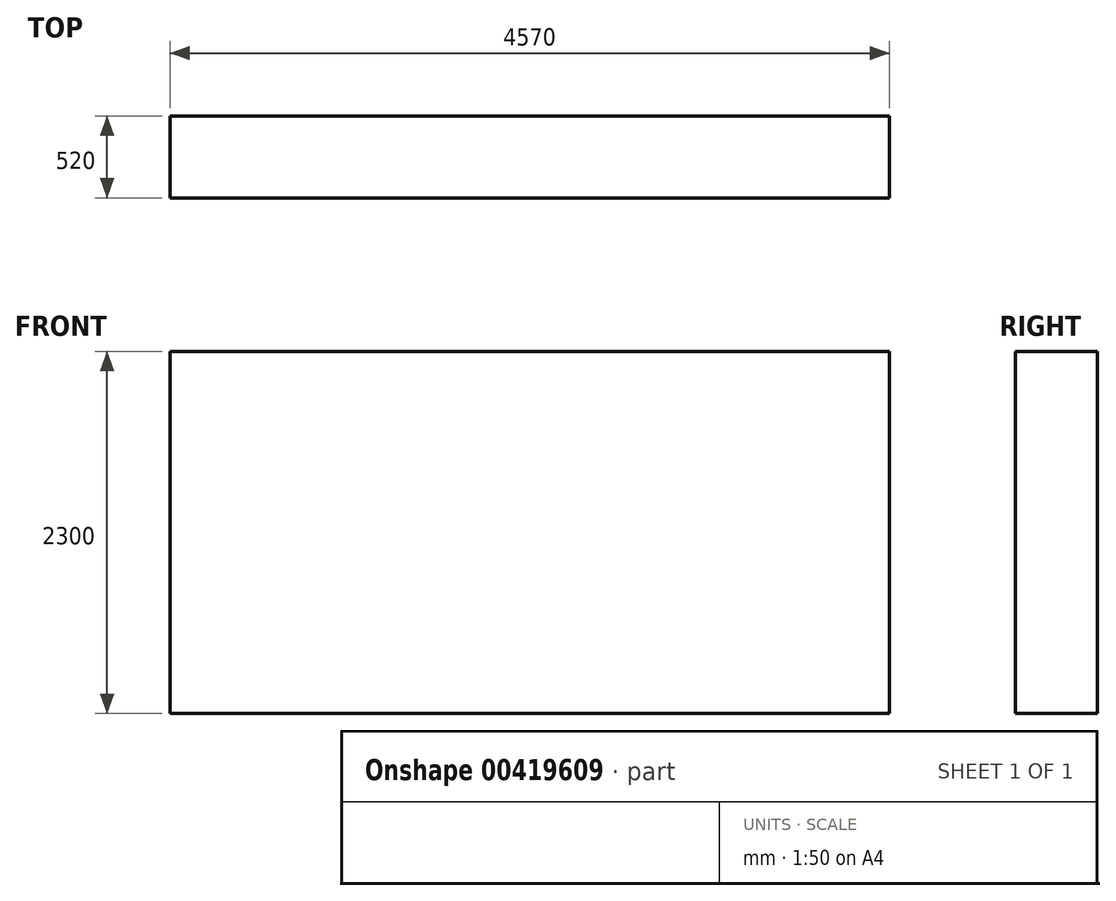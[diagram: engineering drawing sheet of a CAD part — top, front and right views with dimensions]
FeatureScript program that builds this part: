
annotation { "Feature Type Name" : "Feature", "Feature Type Description" : "" }
export const myFeature = defineFeature(function(context is Context, id is Id, definition is map)
    precondition{}
    {
        {
            var Q0;
            Q0=qCreatedBy(makeId("Top.planeOp"),FACE);
            var sketch = newSketch(context, id + "F0", { "sketchPlane" : qUnion([Q0])});
            skLineSegment(sketch, "E0.bottom", {"start": v(-4448.4, 487.42) * mm, "end": v(121.6, 487.42) * mm});
            skLineSegment(sketch, "E0.top", {"start": v(-4448.4, -32.58) * mm, "end": v(121.6, -32.58) * mm});
            skLineSegment(sketch, "E0.left", {"start": v(-4448.4, 487.42) * mm, "end": v(-4448.4, -32.58) * mm});
            skLineSegment(sketch, "E0.right", {"start": v(121.6, 487.42) * mm, "end": v(121.6, -32.58) * mm});
            skSolve(sketch);
        }
        {
            var Q0;
            Q0=makeQuery(id+"F0.imprint","IMPRINT",FACE,{"disambiguationData":[TD([[makeQuery(id+"F0.imprint","IMPRINT",EDGE,{"derivedFrom":sQuery(id+"F0.wireOp",EDGE,"E0.bottom")}),-1.0]])]});
            extrude(context, id + "F1", {"entities" : qUnion([Q0]), "depth" : 2300 * mm});
        }
    });
